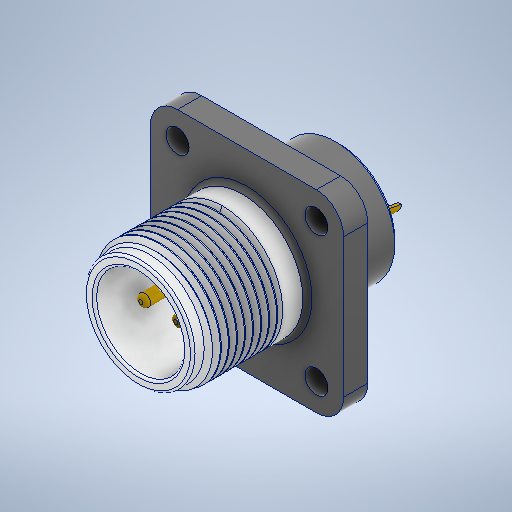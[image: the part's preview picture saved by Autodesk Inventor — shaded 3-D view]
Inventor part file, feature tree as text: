
AUTODESK INVENTOR PART (.ipt)
format: ipt  version: 2025 (Build 290162000, 162)  size: 791,552 bytes
history: native  units: mm
features: fillet x1, mirror x1, boolean_combine x1, other x1
ambient origin geometry x8: Origin, YZ Plane, XZ Plane, XY Plane, X Axis, Y Axis, Z Axis, Center Point
bodies: Solid1 (feature_tree), Solid2 (feature_tree), Solid3 (feature_tree), Solid4 (feature_tree)
feature tree (4):
  fillet  "Fillet3"  [1 undecoded]
  mirror  "Mirror3"
  boolean_combine  "Combine2"
  other  "Boss-Extrude3"
note: 1 required parameter value undecoded (feature->parameter linkage not recoverable at this tier; creation-order binding heuristic only, values carry confidence <= 0.55)
